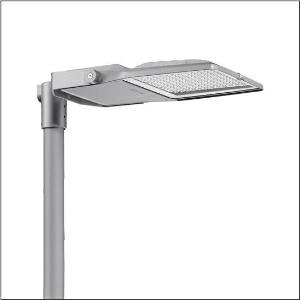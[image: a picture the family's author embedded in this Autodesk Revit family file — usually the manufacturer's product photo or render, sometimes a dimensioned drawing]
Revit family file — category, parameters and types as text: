
# Revit family: floodlight_fl_21_iq_midi___pl33t_5xa7781f4f3a_8e83
name_source: partatom
category: Lighting Fixtures
units: mm (PartAtom-declared; Revit-internal decimal feet)

## family parameters
Cut with Voids When Loaded = No
Host = Face
Light Source = No
Part Type = Normal
Room Calculation Point = No
Round Connector Dimension = Use Diameter
Shared = No

## types (1)
- --- (1 x LED, 36900 lm, 270.2 W, 4000K)
    Apparent Load = 270 VA
    CIE Flux Codes = 26 75 99 100 100
    Color Rendering = 70
    Color Temperature = 4000K
    Default Elevation = 1800 mm
    Description = Floodlight FL 21 iQ midi, floodlight, primary light control with lens, of PMMA, primary optical cover: protective disc, of toughened safety glass, transparent, light distribution: PL33T, light emission: direct distribution, installation type: surface-mounted, LED, High Power LED, rated luminous flux: 36.900lm, luminous efficacy: 137lm/W, light colour: 740, colour temperature: 4000K, control gear: ECG iQ, control: optimised constant luminous flux control (CLO 2.0), Desk-Remote (wireless, voltage-free reading and setting of iQ features in the workshop via application-optimized NFC function/RFID function), Light-Fading, Smart-Wire, Night-Set, Lumen-Switch, Temp-Guard, Auto-Match, with terminal, 6-pole, mains connection: 220..240V, AC, 50/60Hz, start of lifetime: 270W, end of service life: 287W, reduction: 118W, luminaire housing, of diecast aluminium, powder-coated, Siteco® metallic grey (DB 702S), corrosivity category C5 mid according to DIN EN ISO 12944, sealing non-destructively replaceable, please order mast flange separately, mast bracket, of steel, galvanised, powder-coated, Siteco® metallic grey (DB 702S), protection rating (complete): IP66, insulation class (complete): insulation class II (safety insulation), certification: CE, protection symbol: D, impact resistance: IK08, permissible operating ambient temperature: -40..+40°C, permissible operating ambient temperature for outdoor applications: -40..+50°C, standard: DIN EN 12944, LABS conformity tested according to VDMA 24364:2018-05, packaging unit: 1 piece

Light Distribution: PL33T
    Height = 76 mm
    Lamp = 1 x LED
    Lamp Light Flux = 36900 lm
    Lamp Power = 270.2 W
    Lamp count = 1
    Length = 657 mm
    Luminous efficacy = 137 lm/W
    Manufacturer = Siteco
    ModVariant = No
    Model = 5XA7781F4F3A
    Number of Poles = 1
    OnlyDefault = Yes
    Power Factor = 1
    Product Name = Floodlight FL 21 iQ midi | PL33T
    Product group = floodlight | pylon annexe
    ProductGroupID = 6200
    Protection Class = Protection class II
    Protection Degree = IP 66
    RLX_Detail_Level = 1
    RLX_Emergency_Light_Flux = 0 lm
    RLX_Emergency_Type = 0
    RLX_Emergency_Type_DB = No
    RlxData = <blob elided: 153709 chars, md5=abca287b>
    Socket = socket
    Standby Power = 0 W
    System Light Flux = 36900 lm
    System Power = 270 W
    Type Comments = factory setting: luminous flux: 100 % | dim-lin: 254 | 620 mA
    Type Image = l_1007123.jpg
    URL = http://relux.com
    VarID = @adj_033615
    Voltage = 0 V
    Weight = 0.00 kg
    Width = 442 mm

## geometry (parser evidence)
native form markers: Blend x4, Sweep x12
no freeform markers — native parametric forms only
